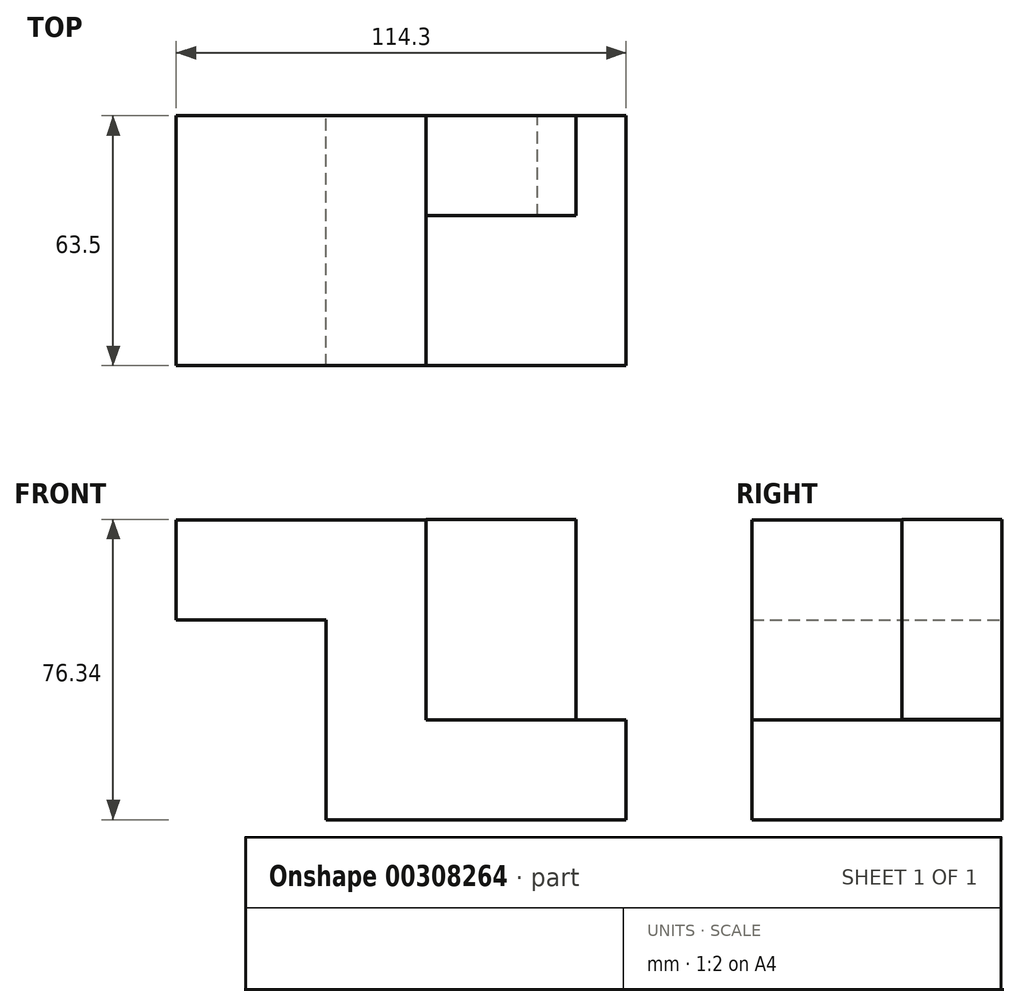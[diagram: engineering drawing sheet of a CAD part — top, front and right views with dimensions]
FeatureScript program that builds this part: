
annotation { "Feature Type Name" : "Feature", "Feature Type Description" : "" }
export const myFeature = defineFeature(function(context is Context, id is Id, definition is map)
    precondition{}
    {
        {
            var Q0;
            Q0=qCreatedBy(makeId("Front.planeOp"),FACE);
            var sketch = newSketch(context, id + "F0", { "sketchPlane" : qUnion([Q0])});
            skLineSegment(sketch, "E0", {"start": v(-78.56, 50.63) * mm, "end": v(-40.46, 50.63) * mm});
            skLineSegment(sketch, "E1", {"start": v(-40.46, 50.63) * mm, "end": v(-40.46, -0.17) * mm});
            skLineSegment(sketch, "E2", {"start": v(-40.46, -0.17) * mm, "end": v(35.74, -0.17) * mm});
            skLineSegment(sketch, "E3", {"start": v(35.74, -0.17) * mm, "end": v(35.74, 25.23) * mm});
            skLineSegment(sketch, "E4", {"start": v(35.74, 25.23) * mm, "end": v(-15.06, 25.23) * mm});
            skLineSegment(sketch, "E5", {"start": v(-15.06, 25.23) * mm, "end": v(-15.06, 76.03) * mm});
            skLineSegment(sketch, "E6", {"start": v(-15.06, 76.03) * mm, "end": v(-78.56, 76.03) * mm});
            skLineSegment(sketch, "E7", {"start": v(-78.56, 76.03) * mm, "end": v(-78.56, 50.63) * mm});
            skSolve(sketch);
        }
        {
            var Q0;
            Q0=makeQuery(id+"F0.imprint","IMPRINT",FACE,{"disambiguationData":[TD([[makeQuery(id+"F0.imprint","IMPRINT",EDGE,{"derivedFrom":sQuery(id+"F0.wireOp",EDGE,"E0")}),1.0]])]});
            extrude(context, id + "F1", {"entities" : qUnion([Q0]), "depth" : 63.5 * mm});
        }
        {
            var Q0;
            Q0=qCreatedBy(makeId("Front.planeOp"),FACE);
            var sketch = newSketch(context, id + "F2", { "sketchPlane" : qUnion([Q0])});
            skLineSegment(sketch, "E8", {"start": v(23.03, 25.37) * mm, "end": v(23.03, 76.17) * mm});
            skLineSegment(sketch, "E9", {"start": v(23.03, 76.17) * mm, "end": v(-15.07, 76.17) * mm});
            skLineSegment(sketch, "E10", {"start": v(-15.07, 76.17) * mm, "end": v(-15.07, 24.8) * mm});
            skLineSegment(sketch, "E11", {"start": v(-15.07, 24.8) * mm, "end": v(23.03, 25.37) * mm});
            skSolve(sketch);
        }
        {
            var Q0;
            Q0=makeQuery(id+"F2.imprint","IMPRINT",FACE,{"disambiguationData":[TD([[makeQuery(id+"F2.imprint","IMPRINT",EDGE,{"derivedFrom":sQuery(id+"F2.wireOp",EDGE,"E8")}),1.0]])]});
            extrude(context, id + "F3", {"entities" : qUnion([Q0]), "operationType" : NewBodyOperationType.ADD, "depth" : 25.4 * mm});
        }
    });
